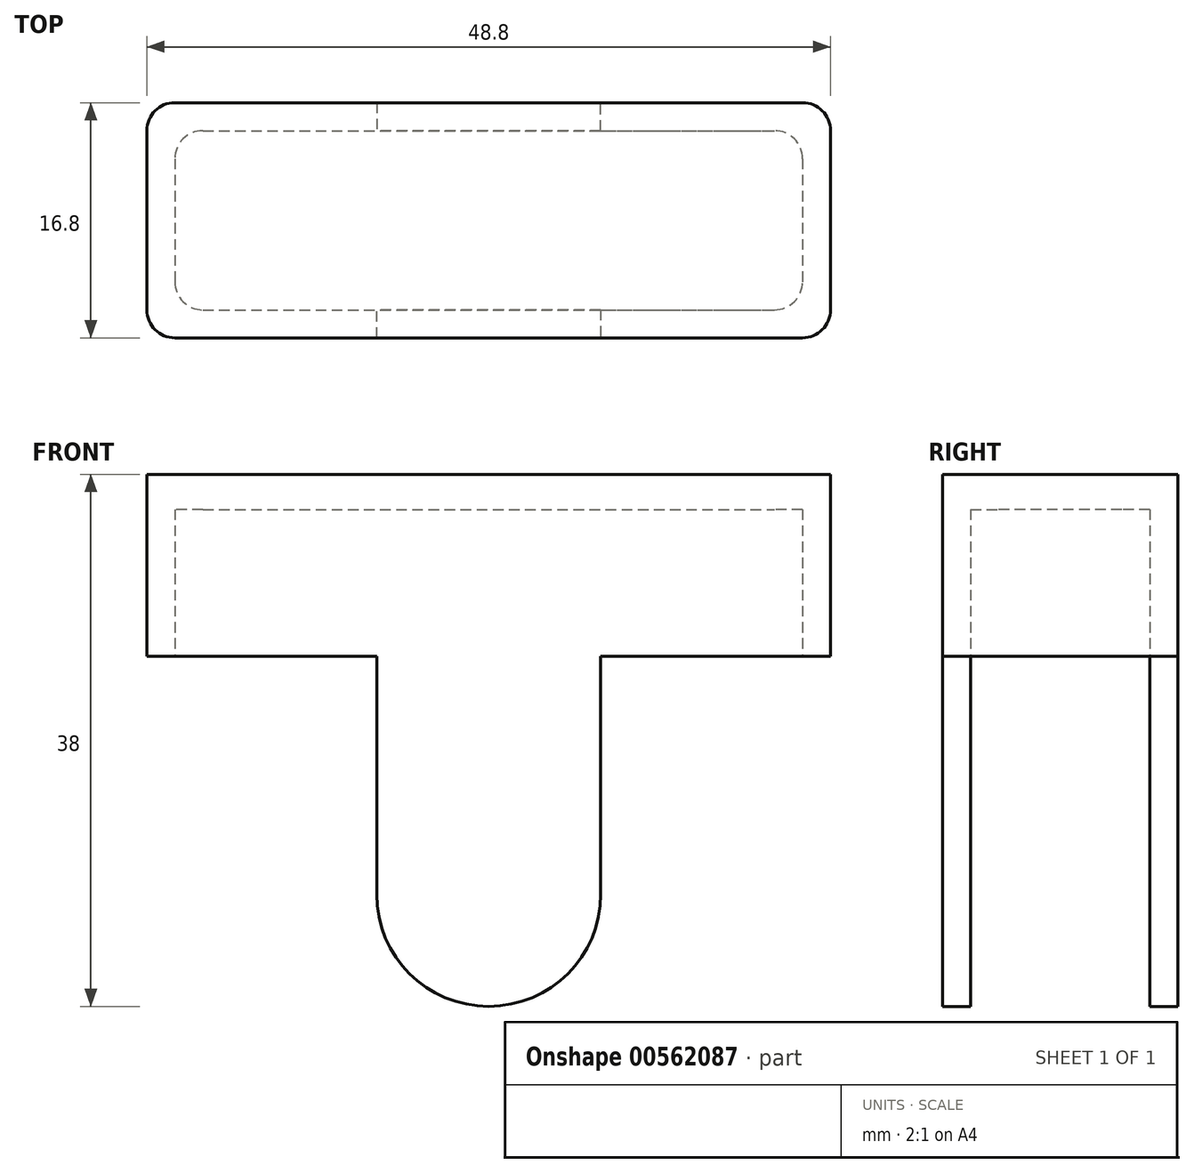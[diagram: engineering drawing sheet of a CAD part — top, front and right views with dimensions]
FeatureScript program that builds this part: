
annotation { "Feature Type Name" : "Feature", "Feature Type Description" : "" }
export const myFeature = defineFeature(function(context is Context, id is Id, definition is map)
    precondition{}
    {
        {
            var Q0;
            Q0=qCreatedBy(makeId("Top.planeOp"),FACE);
            var sketch = newSketch(context, id + "F0", { "sketchPlane" : qUnion([Q0])});
            skLineSegment(sketch, "E0.bottom", {"start": v(-20, 4) * mm, "end": v(20, 4) * mm});
            skLineSegment(sketch, "E0.top", {"start": v(-20, -4) * mm, "end": v(20, -4) * mm});
            skLineSegment(sketch, "E0.left", {"start": v(-20, 4) * mm, "end": v(-20, -4) * mm});
            skLineSegment(sketch, "E0.right", {"start": v(20, 4) * mm, "end": v(20, -4) * mm});
            skLineSegment(sketch, "E1.0", {"start": v(-22, 6) * mm, "end": v(-22, -6) * mm});
            skLineSegment(sketch, "E1.1", {"start": v(-22, 6) * mm, "end": v(22, 6) * mm});
            skLineSegment(sketch, "E1.2", {"start": v(22, 6) * mm, "end": v(22, -6) * mm});
            skLineSegment(sketch, "E1.3", {"start": v(-22, -6) * mm, "end": v(22, -6) * mm});
            skLineSegment(sketch, "E2.0", {"start": v(-22.4, 6.4) * mm, "end": v(-22.4, -6.4) * mm});
            skLineSegment(sketch, "E2.1", {"start": v(-22.4, 6.4) * mm, "end": v(22.4, 6.4) * mm});
            skLineSegment(sketch, "E2.2", {"start": v(22.4, 6.4) * mm, "end": v(22.4, -6.4) * mm});
            skLineSegment(sketch, "E2.3", {"start": v(-22.4, -6.4) * mm, "end": v(22.4, -6.4) * mm});
            skLineSegment(sketch, "E3.0", {"start": v(-24.4, 8.4) * mm, "end": v(-24.4, -8.4) * mm});
            skLineSegment(sketch, "E3.1", {"start": v(-24.4, 8.4) * mm, "end": v(24.4, 8.4) * mm});
            skLineSegment(sketch, "E3.2", {"start": v(24.4, 8.4) * mm, "end": v(24.4, -8.4) * mm});
            skLineSegment(sketch, "E3.3", {"start": v(-24.4, -8.4) * mm, "end": v(24.4, -8.4) * mm});
            skSolve(sketch);
        }
        {
            var Q0;
            Q0=makeQuery(id+"F0.imprint","IMPRINT",FACE,{"disambiguationData":[TD([[makeQuery(id+"F0.imprint","IMPRINT",EDGE,{"derivedFrom":sQuery(id+"F0.wireOp",EDGE,"E2.0")}),-1.0]])]});
            var Q1;
            Q1=makeQuery(id+"F0.imprint","IMPRINT",FACE,{"disambiguationData":[TD([[makeQuery(id+"F0.imprint","IMPRINT",EDGE,{"derivedFrom":sQuery(id+"F0.wireOp",EDGE,"E1.0")}),-1.0]])]});
            var Q2;
            Q2=makeQuery(id+"F0.imprint","IMPRINT",FACE,{"disambiguationData":[TD([[makeQuery(id+"F0.imprint","IMPRINT",EDGE,{"derivedFrom":sQuery(id+"F0.wireOp",EDGE,"E0.bottom")}),1.0]])]});
            var Q3;
            Q3=makeQuery(id+"F0.imprint","IMPRINT",FACE,{"disambiguationData":[TD([[makeQuery(id+"F0.imprint","IMPRINT",EDGE,{"derivedFrom":sQuery(id+"F0.wireOp",EDGE,"E0.bottom")}),-1.0]])]});
            extrude(context, id + "F1", {"entities" : qUnion([Q0, Q1, Q2, Q3]), "depth" : 13 * mm, "offsetDistance" : 25 * mm});
        }
        {
            var Q0;
            Q0=makeQuery(id+"F0.imprint","IMPRINT",FACE,{"disambiguationData":[TD([[makeQuery(id+"F0.imprint","IMPRINT",EDGE,{"derivedFrom":sQuery(id+"F0.wireOp",EDGE,"E0.bottom")}),-1.0]])]});
            var Q1;
            Q1=makeQuery(id+"F0.imprint","IMPRINT",FACE,{"disambiguationData":[TD([[makeQuery(id+"F0.imprint","IMPRINT",EDGE,{"derivedFrom":sQuery(id+"F0.wireOp",EDGE,"E0.bottom")}),1.0]])]});
            var Q2;
            Q2=makeQuery(id+"F0.imprint","IMPRINT",FACE,{"disambiguationData":[TD([[makeQuery(id+"F0.imprint","IMPRINT",EDGE,{"derivedFrom":sQuery(id+"F0.wireOp",EDGE,"E1.0")}),-1.0]])]});
            extrude(context, id + "F2", {"entities" : qUnion([Q0, Q1, Q2]), "operationType" : NewBodyOperationType.REMOVE, "depth" : 10.5 * mm, "offsetDistance" : 25 * mm});
        }
        {
            var Q0;
            Q0=makeQuery(id+"F1.opExtrude","SWEPT_EDGE",EDGE,{"disambiguationData":[OSD([sQuery(id+"F0.wireOp",EDGE,"E3.0"),sQuery(id+"F0.wireOp",EDGE,"E3.3")])]});
            var Q1;
            Q1=makeQuery(id+"F1.opExtrude","SWEPT_EDGE",EDGE,{"disambiguationData":[OSD([sQuery(id+"F0.wireOp",EDGE,"E3.0"),sQuery(id+"F0.wireOp",EDGE,"E3.1")])]});
            var Q2;
            Q2=makeQuery(id+"F1.opExtrude","SWEPT_EDGE",EDGE,{"disambiguationData":[OSD([sQuery(id+"F0.wireOp",EDGE,"E3.2"),sQuery(id+"F0.wireOp",EDGE,"E3.3")])]});
            var Q3;
            Q3=makeQuery(id+"F1.opExtrude","SWEPT_EDGE",EDGE,{"disambiguationData":[OSD([sQuery(id+"F0.wireOp",EDGE,"E3.1"),sQuery(id+"F0.wireOp",EDGE,"E3.2")])]});
            fillet(context, id + "F3", {"entities" : qUnion([Q0, Q1, Q2, Q3]), "radius" : 2 * mm, "tangentPropagation" : true, "allowEdgeOverflow" : false});
        }
        {
            var Q0;
            Q0=makeQuery(id+"F2.boolean.opBoolean","COPY",EDGE,{"derivedFrom":makeQuery(id+"F2.opExtrude","SWEPT_EDGE",EDGE,{"disambiguationData":[OSD([sQuery(id+"F0.wireOp",EDGE,"E2.0"),sQuery(id+"F0.wireOp",EDGE,"E2.3")])]})});
            var Q1;
            Q1=makeQuery(id+"F2.boolean.opBoolean","COPY",EDGE,{"derivedFrom":makeQuery(id+"F2.opExtrude","SWEPT_EDGE",EDGE,{"disambiguationData":[OSD([sQuery(id+"F0.wireOp",EDGE,"E2.2"),sQuery(id+"F0.wireOp",EDGE,"E2.3")])]})});
            var Q2;
            Q2=makeQuery(id+"F2.boolean.opBoolean","COPY",EDGE,{"derivedFrom":makeQuery(id+"F2.opExtrude","SWEPT_EDGE",EDGE,{"disambiguationData":[OSD([sQuery(id+"F0.wireOp",EDGE,"E2.1"),sQuery(id+"F0.wireOp",EDGE,"E2.2")])]})});
            var Q3;
            Q3=makeQuery(id+"F2.boolean.opBoolean","COPY",EDGE,{"derivedFrom":makeQuery(id+"F2.opExtrude","SWEPT_EDGE",EDGE,{"disambiguationData":[OSD([sQuery(id+"F0.wireOp",EDGE,"E2.0"),sQuery(id+"F0.wireOp",EDGE,"E2.1")])]})});
            fillet(context, id + "F4", {"entities" : qUnion([Q0, Q1, Q2, Q3]), "radius" : 2 * mm, "tangentPropagation" : true, "allowEdgeOverflow" : false});
        }
        {
            var Q0;
            Q0=makeQuery(id+"F1.opExtrude","CAP_FACE",FACE,{"disambiguationData":[OSD([sQuery(id+"F0.wireOp",EDGE,"E3.0"),sQuery(id+"F0.wireOp",EDGE,"E3.1"),sQuery(id+"F0.wireOp",EDGE,"E3.2"),sQuery(id+"F0.wireOp",EDGE,"E3.3")])],"isStart":true});
            var sketch = newSketch(context, id + "F5", { "sketchPlane" : qUnion([Q0])});
            skLineSegment(sketch, "E4", {"start": v(0, 6.4) * mm, "end": v(8, 6.4) * mm});
            skLineSegment(sketch, "E5", {"start": v(8, 6.4) * mm, "end": v(8, 8.4) * mm});
            skLineSegment(sketch, "E6", {"start": v(8, 8.4) * mm, "end": v(-8, 8.4) * mm});
            skLineSegment(sketch, "E7", {"start": v(-8, 8.4) * mm, "end": v(-8, 6.4) * mm});
            skLineSegment(sketch, "E8", {"start": v(-8, 6.4) * mm, "end": v(0, 6.4) * mm});
            skLineSegment(sketch, "E9", {"start": v(0, -6.4) * mm, "end": v(8, -6.4) * mm});
            skLineSegment(sketch, "E10", {"start": v(8, -6.4) * mm, "end": v(8, -8.4) * mm});
            skLineSegment(sketch, "E11", {"start": v(8, -8.4) * mm, "end": v(-8, -8.4) * mm});
            skLineSegment(sketch, "E12", {"start": v(-8, -8.4) * mm, "end": v(-8, -6.4) * mm});
            skLineSegment(sketch, "E13", {"start": v(-8, -6.4) * mm, "end": v(0, -6.4) * mm});
            skSolve(sketch);
        }
        {
            var Q0;
            Q0=makeQuery(id+"F5.imprint","IMPRINT",FACE,{"disambiguationData":[TD([[makeQuery(id+"F5.imprint","IMPRINT",EDGE,{"derivedFrom":sQuery(id+"F5.wireOp",EDGE,"E4")}),1.0]])]});
            var Q1;
            Q1=makeQuery(id+"F5.imprint","IMPRINT",FACE,{"disambiguationData":[TD([[makeQuery(id+"F5.imprint","IMPRINT",EDGE,{"derivedFrom":sQuery(id+"F5.wireOp",EDGE,"E9")}),-1.0]])]});
            extrude(context, id + "F6", {"entities" : qUnion([Q0, Q1]), "operationType" : NewBodyOperationType.ADD, "depth" : 25 * mm, "offsetDistance" : 25 * mm});
        }
        {
            var Q0;
            Q0=makeQuery(id+"F6.opExtrude","CAP_EDGE",EDGE,{"disambiguationData":[OSD([sQuery(id+"F5.wireOp",EDGE,"E7")])],"isStart":false});
            var Q1;
            Q1=makeQuery(id+"F6.opExtrude","CAP_EDGE",EDGE,{"disambiguationData":[OSD([sQuery(id+"F5.wireOp",EDGE,"E5")])],"isStart":false});
            var Q2;
            Q2=makeQuery(id+"F6.opExtrude","CAP_EDGE",EDGE,{"disambiguationData":[OSD([sQuery(id+"F5.wireOp",EDGE,"E12")])],"isStart":false});
            var Q3;
            Q3=makeQuery(id+"F6.opExtrude","CAP_EDGE",EDGE,{"disambiguationData":[OSD([sQuery(id+"F5.wireOp",EDGE,"E10")])],"isStart":false});
            fillet(context, id + "F7", {"entities" : qUnion([Q0, Q1, Q2, Q3]), "radius" : 8 * mm, "tangentPropagation" : true, "allowEdgeOverflow" : false});
        }
    });
